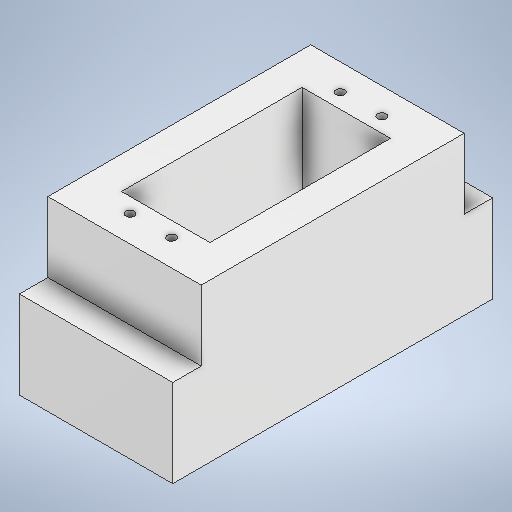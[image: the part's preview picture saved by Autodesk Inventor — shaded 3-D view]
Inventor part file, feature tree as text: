
AUTODESK INVENTOR PART (.ipt)
format: ipt  version: 2025.1 (Build 291241000, 241)  size: 290,816 bytes
history: native  units: mm
features: sketch x6, extrude x5, hole x1
ambient origin geometry x8: Origin, YZ Plane, XZ Plane, XY Plane, X Axis, Y Axis, Z Axis, Center Point
bodies: Solid1 (feature_tree)
feature tree (12):
  extrude  "Extrusion1"  Depth=73.0mm
  extrude  "Extrusion2"  TaperAngle=0.0deg  [1 undecoded]
  extrude  "Extrusion4"  Depth=50.0mm
  extrude  "Extrusion8"  Depth=6.0mm
  extrude  "Extrusion9"  Depth=6.0mm
  hole  "Hole1"  [1 undecoded]
  sketch  "Sketch1"  dims[d0=35.0mm d1=73.0mm]
  sketch  "Sketch2"  dims[d2=6.0mm d3=0.0mm]
  sketch  "Sketch4"  dims[d4=29.0mm d5=50.0mm]
  sketch  "Sketch9"  dims[d9=14.0mm d10=0.0mm d15=6.0mm]
  sketch  "Sketch10"  dims[d16=6.0mm d19=12.0mm]
  sketch  "Sketch12"  dims[d20=30.0mm d21=48.015mm d22=2.8mm d23=4.5mm d24=4.007mm d25=2.8mm d26=6.5mm d27=15.507mm d28=0.0mm d29=0.0mm d45=20.2mm d46=41.2mm d47=16.0mm d48=10.0mm d49=0.0mm d50=0.0mm d51=35.0mm d52=60.0mm d53=0.0mm d54=0.0mm d55=9.5mm d56=48.0mm d57=2.0mm d58=6.0mm d59=4.0mm d60=2.0mm d61=90.0deg d62=15.0mm d63=0.0mm]
note: 2 required parameter values undecoded (feature->parameter linkage not recoverable at this tier; creation-order binding heuristic only, values carry confidence <= 0.55)
